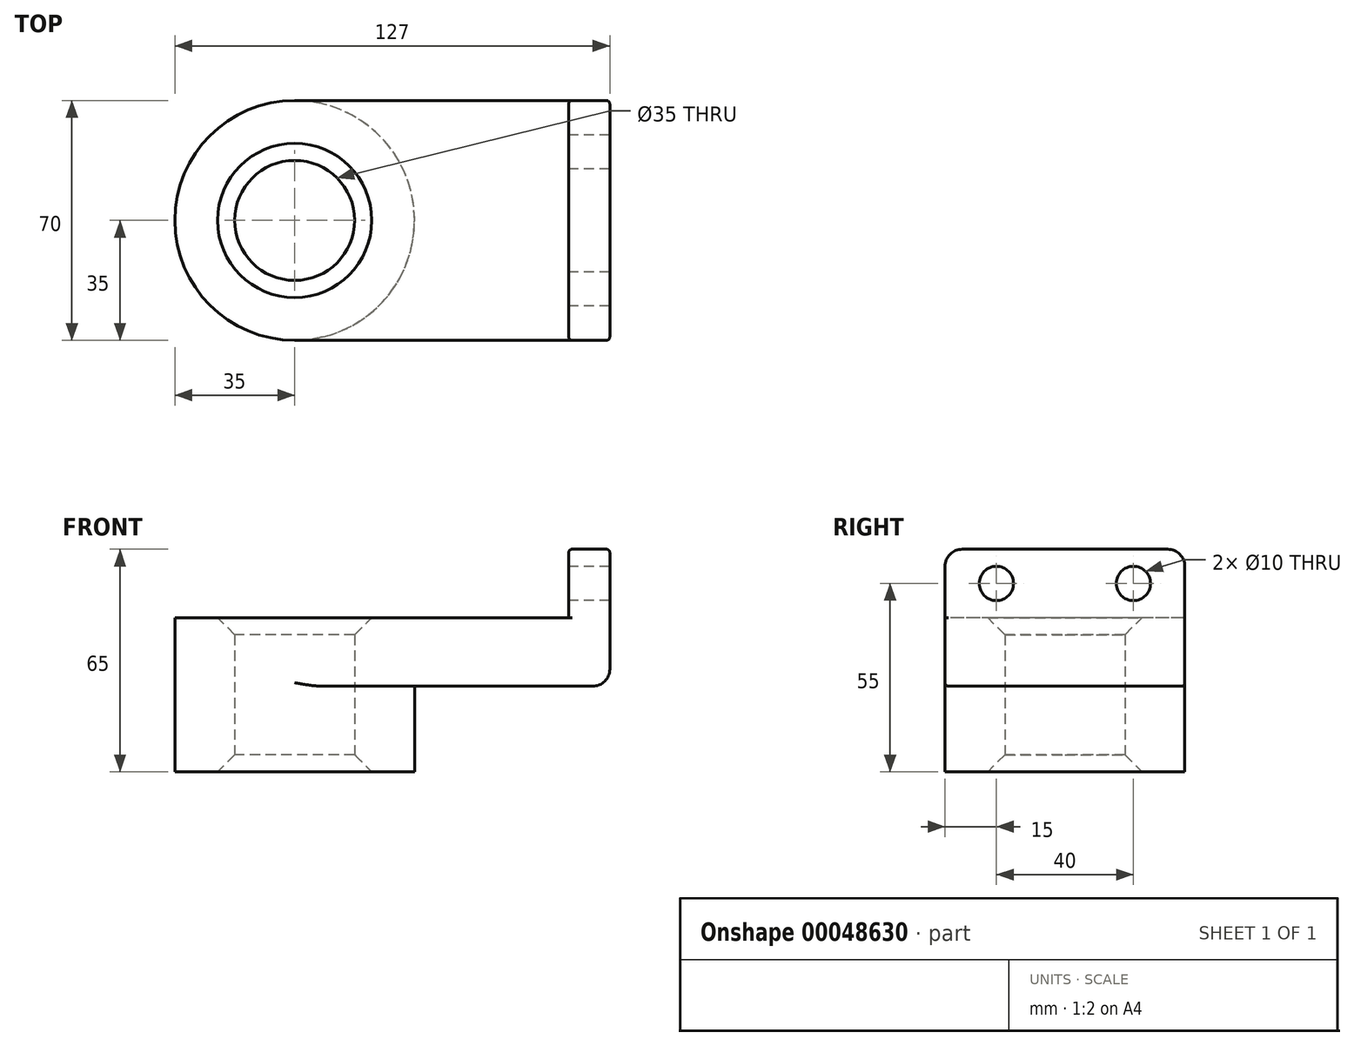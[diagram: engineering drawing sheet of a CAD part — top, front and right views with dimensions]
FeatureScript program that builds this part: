
annotation { "Feature Type Name" : "Feature", "Feature Type Description" : "" }
export const myFeature = defineFeature(function(context is Context, id is Id, definition is map)
    precondition{}
    {
        {
            var Q0;
            Q0=qCreatedBy(makeId("Top.planeOp"),FACE);
            var sketch = newSketch(context, id + "F0", { "sketchPlane" : qUnion([Q0])});
            skLineSegment(sketch, "E0.rect.bottom", {"start": v(40, 35) * mm, "end": v(-40, 35) * mm});
            skLineSegment(sketch, "E0.rect.top", {"start": v(40, -35) * mm, "end": v(-40, -35) * mm});
            skLineSegment(sketch, "E0.rect.left", {"start": v(40, 35) * mm, "end": v(40, -35) * mm});
            skLineSegment(sketch, "E0.rect.right", {"start": v(-40, 35) * mm, "end": v(-40, -35) * mm});
            skPoint(sketch, "E0.rect.middle", {"position": v(0, 0) * mm});
            skCircle(sketch, "E1", {"center": v(-40, 0) * mm, "radius": 35 * mm});
            skCircle(sketch, "E2", {"center": v(-40, 0) * mm, "radius": 17.5 * mm});
            skSolve(sketch);
        }
        {
            var Q0;
            {var subQ1=sQuery(id+"F0.wireOp",EDGE,"E0.rect.right");var subQ3=sQuery(id+"F0.wireOp",EDGE,"E2");var subQ4=makeQuery(id+"F0.imprint","INTERSECT",VERTEX,{"disambiguationData":[OD(0.0)],"derivedFrom":[subQ1,subQ3]});Q0=makeQuery(id+"F0.imprint","IMPRINT",FACE,{"disambiguationData":[TD([[makeQuery(id+"F0.imprint","IMPRINT",EDGE,{"disambiguationData":[TD([[subQ4,-1.0]])],"derivedFrom":subQ3}),-1.0]])]});}
            var Q1;
            {var subQ1=sQuery(id+"F0.wireOp",EDGE,"E0.rect.right");var subQ3=sQuery(id+"F0.wireOp",EDGE,"E2");var subQ4=makeQuery(id+"F0.imprint","INTERSECT",VERTEX,{"disambiguationData":[OD(0.0)],"derivedFrom":[subQ1,subQ3]});Q1=makeQuery(id+"F0.imprint","IMPRINT",FACE,{"disambiguationData":[TD([[makeQuery(id+"F0.imprint","IMPRINT",EDGE,{"disambiguationData":[TD([[subQ4,1.0]])],"derivedFrom":subQ3}),-1.0]])]});}
            var Q2;
            {var subQ0=sQuery(id+"F0.wireOp",EDGE,"E0.rect.bottom");Q2=makeQuery(id+"F0.imprint","IMPRINT",FACE,{"disambiguationData":[TD([[makeQuery(id+"F0.imprint","IMPRINT",EDGE,{"derivedFrom":subQ0}),1.0]])]});}
            extrude(context, id + "F1", {"entities" : qUnion([Q0, Q1, Q2]), "depth" : 20 * mm});
        }
        {
            var Q0;
            {var subQ1=sQuery(id+"F0.wireOp",EDGE,"E0.rect.right");var subQ3=sQuery(id+"F0.wireOp",EDGE,"E2");var subQ4=makeQuery(id+"F0.imprint","INTERSECT",VERTEX,{"disambiguationData":[OD(0.0)],"derivedFrom":[subQ1,subQ3]});Q0=makeQuery(id+"F0.imprint","IMPRINT",FACE,{"disambiguationData":[TD([[makeQuery(id+"F0.imprint","IMPRINT",EDGE,{"disambiguationData":[TD([[subQ4,-1.0]])],"derivedFrom":subQ3}),-1.0]])]});}
            var Q1;
            {var subQ1=sQuery(id+"F0.wireOp",EDGE,"E0.rect.right");var subQ3=sQuery(id+"F0.wireOp",EDGE,"E2");var subQ4=makeQuery(id+"F0.imprint","INTERSECT",VERTEX,{"disambiguationData":[OD(0.0)],"derivedFrom":[subQ1,subQ3]});Q1=makeQuery(id+"F0.imprint","IMPRINT",FACE,{"disambiguationData":[TD([[makeQuery(id+"F0.imprint","IMPRINT",EDGE,{"disambiguationData":[TD([[subQ4,1.0]])],"derivedFrom":subQ3}),-1.0]])]});}
            extrude(context, id + "F2", {"entities" : qUnion([Q0, Q1]), "operationType" : NewBodyOperationType.ADD, "oppositeDirection" : true, "depth" : 25 * mm});
        }
        {
            var Q0;
            Q0=makeQuery(id+"F1.opExtrude","SWEPT_FACE",FACE,{"disambiguationData":[OSD([sQuery(id+"F0.wireOp",EDGE,"E0.rect.left")])]});
            var sketch = newSketch(context, id + "F3", { "sketchPlane" : qUnion([Q0])});
            skLineSegment(sketch, "E3.bottom", {"start": v(35, 0) * mm, "end": v(-35, 0) * mm});
            skLineSegment(sketch, "E3.top", {"start": v(35, 40) * mm, "end": v(-35, 40) * mm});
            skLineSegment(sketch, "E3.left", {"start": v(35, 0) * mm, "end": v(35, 40) * mm});
            skLineSegment(sketch, "E3.right", {"start": v(-35, 0) * mm, "end": v(-35, 40) * mm});
            skCircle(sketch, "E4", {"center": v(20, 30) * mm, "radius": 5 * mm});
            skLineSegment(sketch, "E5", {"start": v(0, 40) * mm, "end": v(0, -33) * mm, "construction": true});
            skPoint(sketch, "E5.endSnap0", {"position": v(0, 40) * mm});
            skCircle(sketch, "E6.MirrorC", {"center": v(-20, 30) * mm, "radius": 5 * mm});
            skSolve(sketch);
        }
        {
            var Q0;
            {var subQ0=sQuery(id+"F3.wireOp",EDGE,"E3.bottom");Q0=makeQuery(id+"F3.imprint","IMPRINT",FACE,{"disambiguationData":[TD([[makeQuery(id+"F3.imprint","IMPRINT",EDGE,{"derivedFrom":subQ0}),-1.0]])]});}
            var Q1;
            {var subQ2=sQuery(id+"F3.wireOp",EDGE,"E3.top");Q1=makeQuery(id+"F3.imprint","IMPRINT",FACE,{"disambiguationData":[TD([[makeQuery(id+"F3.imprint","IMPRINT",EDGE,{"derivedFrom":subQ2}),1.0]])]});}
            extrude(context, id + "F4", {"entities" : qUnion([Q0, Q1]), "operationType" : NewBodyOperationType.ADD, "depth" : 12 * mm});
        }
        {
            var Q0;
            Q0=makeQuery(id+"F4.opExtrude","CAP_EDGE",EDGE,{"disambiguationData":[OSD([sQuery(id+"F3.wireOp",EDGE,"E3.bottom")])],"isStart":false});
            var Q1;
            Q1=makeQuery(id+"F2.opExtrude","CAP_EDGE",EDGE,{"disambiguationData":[OSD([sQuery(id+"F0.wireOp",EDGE,"E1")])],"isStart":true});
            var Q2;
            Q2=makeQuery(id+"F4.opExtrude","SWEPT_EDGE",EDGE,{"disambiguationData":[OSD([sQuery(id+"F3.wireOp",EDGE,"E3.top"),sQuery(id+"F3.wireOp",EDGE,"E3.left")])]});
            var Q3;
            Q3=makeQuery(id+"F4.opExtrude","SWEPT_EDGE",EDGE,{"disambiguationData":[OSD([sQuery(id+"F3.wireOp",EDGE,"E3.top"),sQuery(id+"F3.wireOp",EDGE,"E3.right")])]});
            fillet(context, id + "F5", {"entities" : qUnion([Q0, Q1, Q2, Q3]), "radius" : 5 * mm, "tangentPropagation" : true, "allowEdgeOverflow" : false});
        }
        {
            var Q0;
            {var subQ0=sQuery(id+"F0.wireOp",EDGE,"E2");Q0=makeQuery(id+"F2.boolean.opBoolean","MERGE",FACE,{"derivedFrom":[makeQuery(id+"F1.opExtrude","SWEPT_FACE",FACE,{"disambiguationData":[OSD([subQ0])]}),makeQuery(id+"F2.opExtrude","SWEPT_FACE",FACE,{"disambiguationData":[OSD([subQ0])]})]});}
            chamfer(context, id + "F6", {"entities" : qUnion([Q0]), "chamferType" : ChamferType.OFFSET_ANGLE, "width" : 5 * mm, "oppositeDirection" : false, "angle" : 45 * degree, "tangentPropagation" : true});
        }
        {
            var Q0;
            Q0=makeQuery(id+"F4.opExtrude","CAP_EDGE",EDGE,{"disambiguationData":[OSD([sQuery(id+"F3.wireOp",EDGE,"E3.top")])],"isStart":false});
            var Q1;
            Q1=makeQuery(id+"F4.opExtrude","CAP_EDGE",EDGE,{"disambiguationData":[OSD([sQuery(id+"F3.wireOp",EDGE,"E3.top")])],"isStart":true});
            var Q2;
            Q2=makeQuery(id+"F1.opExtrude","CAP_EDGE",EDGE,{"disambiguationData":[OSD([sQuery(id+"F0.wireOp",EDGE,"E0.rect.left")])],"isStart":false});
            fillet(context, id + "F7", {"entities" : qUnion([Q0, Q1, Q2]), "radius" : 1 * mm, "tangentPropagation" : true, "allowEdgeOverflow" : false});
        }
    });
